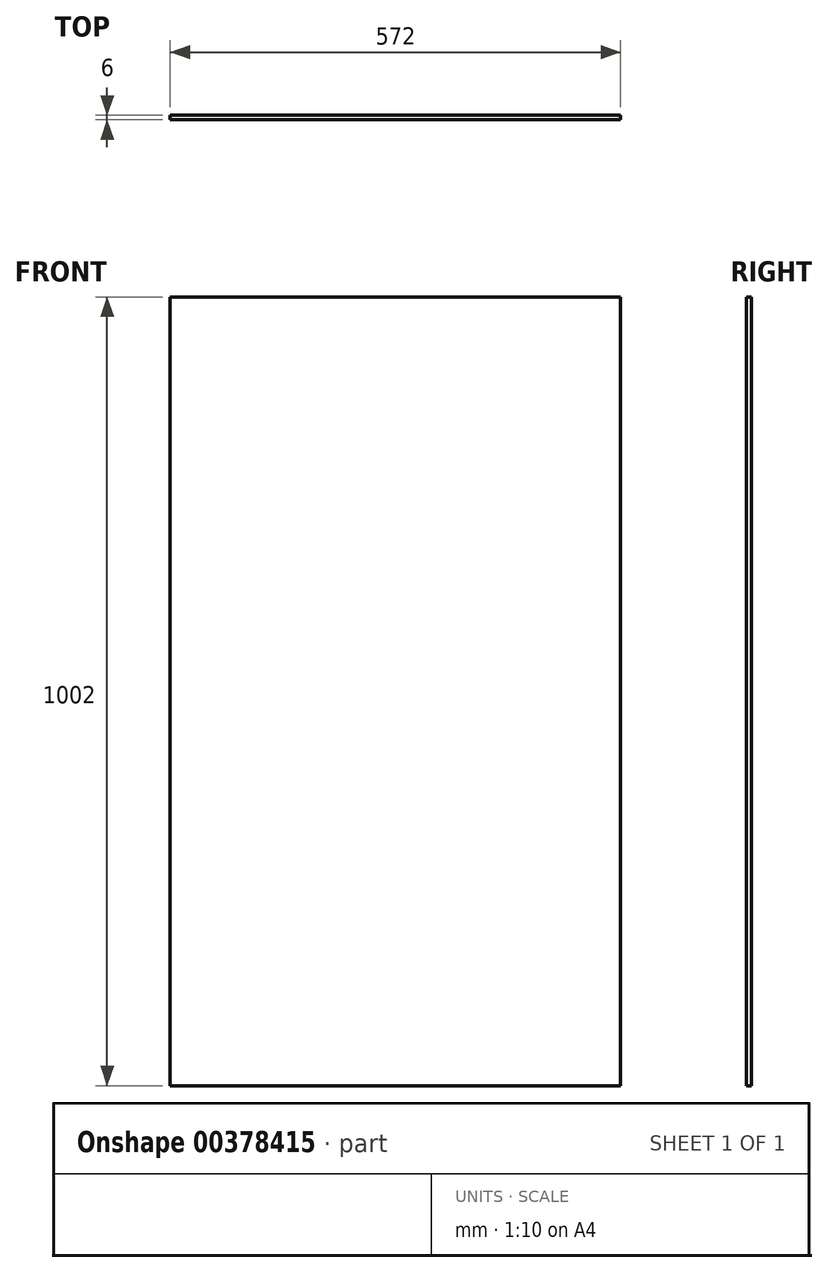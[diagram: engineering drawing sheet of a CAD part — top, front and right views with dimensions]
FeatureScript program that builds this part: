
annotation { "Feature Type Name" : "Feature", "Feature Type Description" : "" }
export const myFeature = defineFeature(function(context is Context, id is Id, definition is map)
    precondition{}
    {
        {
            var Q0;
            Q0=qCreatedBy(makeId("Front.planeOp"),FACE);
            var sketch = newSketch(context, id + "F0", { "sketchPlane" : qUnion([Q0])});
            skLineSegment(sketch, "E0.bottom", {"start": v(286, 501) * mm, "end": v(-286, 501) * mm});
            skLineSegment(sketch, "E0.top", {"start": v(286, -501) * mm, "end": v(-286, -501) * mm});
            skLineSegment(sketch, "E0.left", {"start": v(286, 501) * mm, "end": v(286, -501) * mm});
            skLineSegment(sketch, "E0.right", {"start": v(-286, 501) * mm, "end": v(-286, -501) * mm});
            skPoint(sketch, "E0.middle", {"position": v(0, 0) * mm});
            skSolve(sketch);
        }
        {
            var Q0;
            Q0=makeQuery(id+"F0.imprint","IMPRINT",FACE,{"disambiguationData":[TD([[makeQuery(id+"F0.imprint","IMPRINT",EDGE,{"derivedFrom":sQuery(id+"F0.wireOp",EDGE,"E0.bottom")}),1.0]])]});
            extrude(context, id + "F1", {"entities" : qUnion([Q0]), "depth" : 6 * mm});
        }
    });
